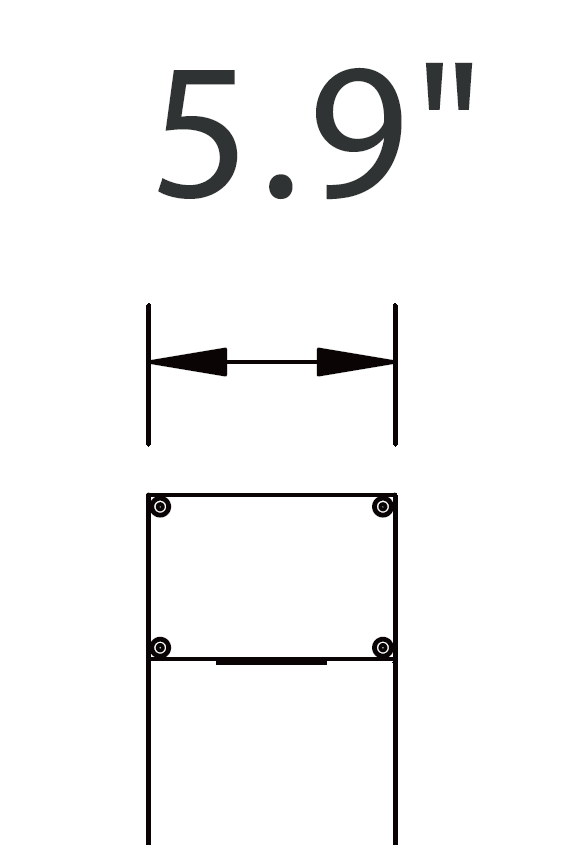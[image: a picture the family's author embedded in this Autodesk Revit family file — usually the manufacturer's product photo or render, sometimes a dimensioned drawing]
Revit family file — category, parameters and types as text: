
# Revit family: Lin2-16.4ft-Double Head
name_source: partatom
category: Lighting Fixtures
units: mm (PartAtom-declared; Revit-internal decimal feet)

## family parameters
Always vertical = Yes
Cut with Voids When Loaded = No
Light Source = No
Maintain Annotation Orientation = No
OmniClass Number = 23.80.70.00
OmniClass Title = Lighting
Part Type = Normal
Room Calculation Point = No
Round Connector Dimension = Use Diameter
Shared = No
Work Plane-Based = No

## types (16) — shared parameters
CRI = 80
Default Elevation = 0' - 0"
H = 16' - 4 13/16"
IP Rating = IP65
Input Voltage = 120-277V
Lamp = LED
Load Classification = Lighting
Manufacturer = Above All Lighting
Power Factor = 0.9
URL = https://www.abovealllighting.com

## per-type parameters (varying)
| type | IES | Model | Wattage Comments |
| LIN2-70W-3000K-II-9.84ft | LIN2 IES : 70W-II | LIN2-7030801-II-BK | 70W |
| LIN2-70W-3000K-III-9.84ft | LIN2 IES : 70W-III | LIN2-7030801-III-BK | 70W |
| LIN2-70W-3000K-IV-9.84ft | LIN2 IES : 70W-IV | LIN2-7030801-IV-BK | 70W |
| LIN2-70W-3000K-V-9.84ft | LIN2 IES : 70W-V | LIN2-7030801-V-BK | 70W |
| LIN2-80W-3000K-II-9.84ft | LIN2 IES : 80W-II | LIN2-8030801-II-BK | 80W |
| LIN2-80W-3000K-III-9.84ft | LIN2 IES : 80W-III | LIN2-8030801-III-BK | 80W |
| LIN2-80W-3000K-IV-9.84ft | LIN2 IES : 80W-IV | LIN2-8030801-IV-BK | 80W |
| LIN2-80W-3000K-V-9.84ft | LIN2 IES : 80W-V | LIN2-8030801-V-BK | 80W |
| LIN2-100W-3000K-II-9.84ft | LIN2 IES : 100W-II | LIN2-10030801-II-BK | 100W |
| LIN2-100W-3000K-III-9.84ft | LIN2 IES : 100W-III | LIN2-10030801-III-BK | 100W |
| LIN2-100W-3000K-IV-9.84ft | LIN2 IES : 100W-IV | LIN2-10030801-IV-BK | 100W |
| LIN2-100W-3000K-V-9.84ft | LIN2 IES : 100W-V | LIN2-10030801-V-BK | 100W |
| LIN2-120W-3000K-II-9.84ft | LIN2 IES : 120W-II | LIN2-12030801-II-BK | 120W |
| LIN2-120W-3000K-III-9.84ft | LIN2 IES : 120W-III | LIN2-12030801-III-BK | 120W |
| LIN2-120W-3000K-IV-9.84ft | LIN2 IES : 120W-IV | LIN2-12030801-IV-BK | 120W |
| LIN2-120W-3000K-V-9.84ft | LIN2 IES : 120W-V | LIN2-12030801-V-BK | 120W |

## geometry (parser evidence)
native form markers: Sweep x3
no freeform markers — native parametric forms only
